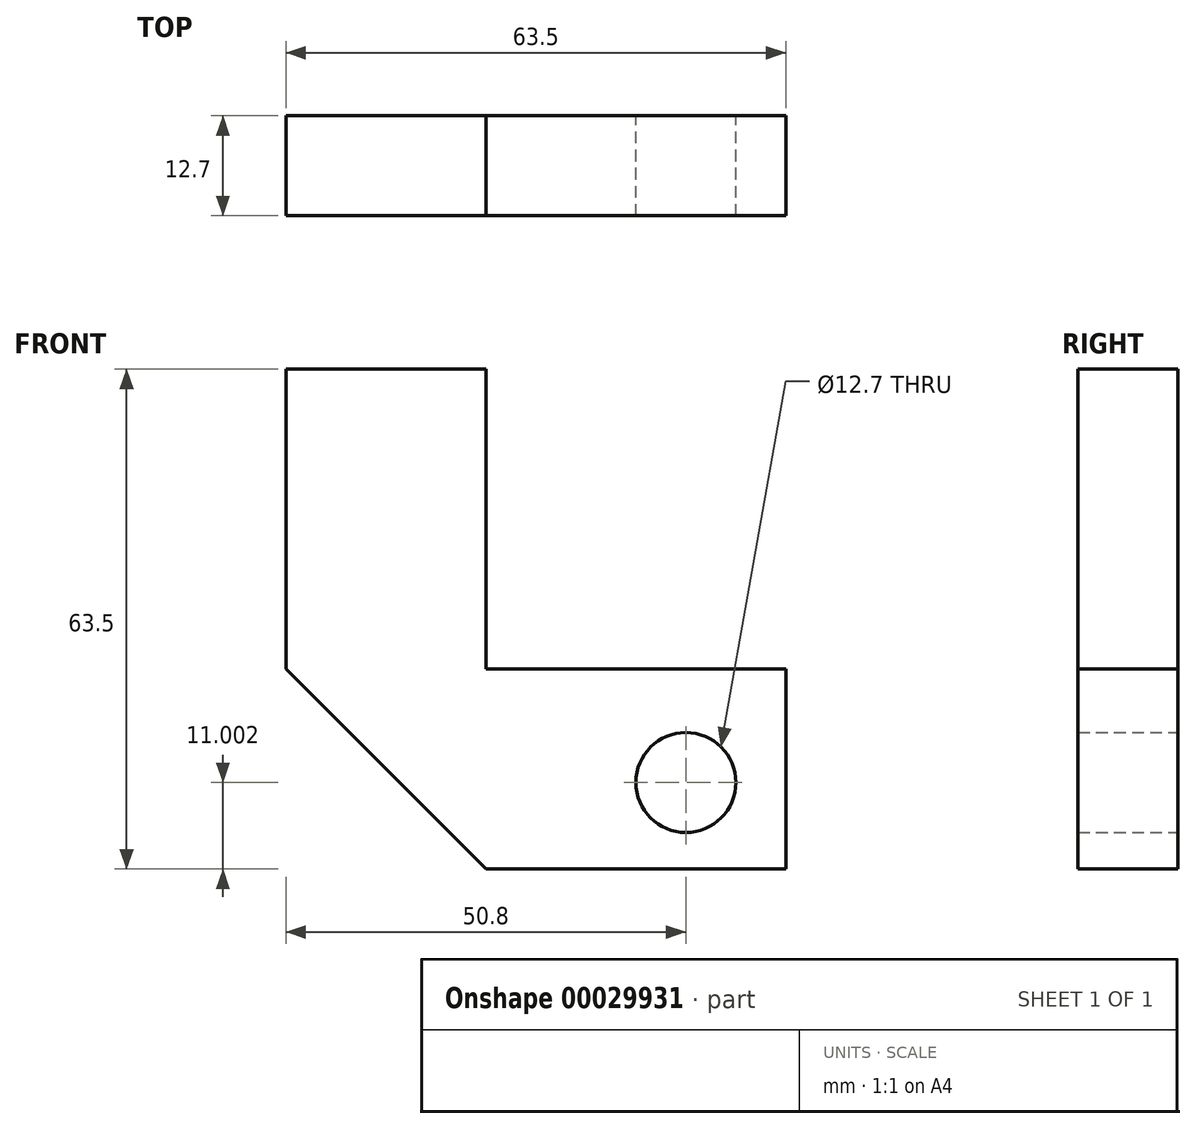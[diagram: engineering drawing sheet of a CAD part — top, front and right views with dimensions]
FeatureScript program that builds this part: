
annotation { "Feature Type Name" : "Feature", "Feature Type Description" : "" }
export const myFeature = defineFeature(function(context is Context, id is Id, definition is map)
    precondition{}
    {
        {
            var Q0;
            Q0=qCreatedBy(makeId("Front.planeOp"),FACE);
            var sketch = newSketch(context, id + "F0", { "sketchPlane" : qUnion([Q0])});
            skLineSegment(sketch, "E0.bottom", {"start": v(39.42, -30.18) * mm, "end": v(77.52, -30.18) * mm});
            skLineSegment(sketch, "E0.top", {"start": v(39.42, -4.78) * mm, "end": v(77.52, -4.78) * mm});
            skLineSegment(sketch, "E0.right", {"start": v(77.52, -30.18) * mm, "end": v(77.52, -4.78) * mm});
            skLineSegment(sketch, "E1.top", {"start": v(14.02, 33.32) * mm, "end": v(39.42, 33.32) * mm});
            skLineSegment(sketch, "E1.left", {"start": v(14.02, -4.78) * mm, "end": v(14.02, 33.32) * mm});
            skLineSegment(sketch, "E1.right", {"start": v(39.42, -4.78) * mm, "end": v(39.42, 33.32) * mm});
            skLineSegment(sketch, "E2", {"start": v(14.02, -4.78) * mm, "end": v(39.42, -30.18) * mm});
            skCircle(sketch, "E3", {"center": v(64.82, -19.18) * mm, "radius": 6.35 * mm});
            skPoint(sketch, "E4.center.orphan", {"position": v(71.17, -19.18) * mm});
            skSolve(sketch);
        }
        {
            var Q0;
            Q0 = qSketchRegion(id + "F0", true);
            extrude(context, id + "F1", {"entities" : qUnion([Q0]), "depth" : 12.7 * mm});
        }
    });
